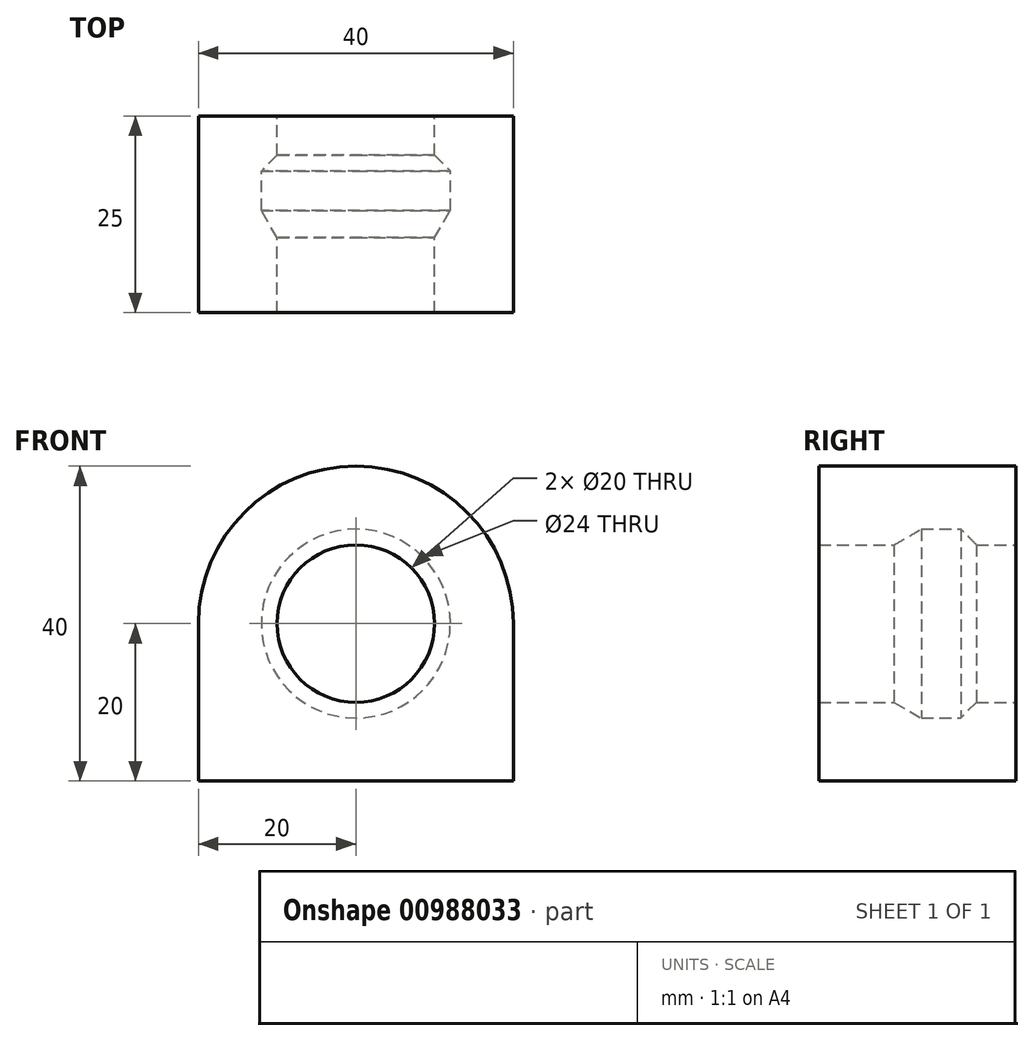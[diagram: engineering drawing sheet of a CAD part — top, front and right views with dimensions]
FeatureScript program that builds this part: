
annotation { "Feature Type Name" : "Feature", "Feature Type Description" : "" }
export const myFeature = defineFeature(function(context is Context, id is Id, definition is map)
    precondition{}
    {
        {
            assignVariable(context, id + "F0", {"name" : "length", "anyValue" : 25});
        }
        {
            var Q0;
            Q0=qCreatedBy(makeId("Front.planeOp"),FACE);
            var sketch = newSketch(context, id + "F1", { "sketchPlane" : qUnion([Q0])});
            skLineSegment(sketch, "E0.top", {"start": v(-20, -20) * mm, "end": v(20, -20) * mm});
            skLineSegment(sketch, "E0.left", {"start": v(-20, 0) * mm, "end": v(-20, -20) * mm});
            skLineSegment(sketch, "E0.right", {"start": v(20, 0) * mm, "end": v(20, -20) * mm});
            skPoint(sketch, "E0.middle", {"position": v(0, 0) * mm});
            skLineSegment(sketch, "E1", {"start": v(0, 0) * mm, "end": v(0, -20) * mm, "construction": true});
            skArc(sketch, "E2", {"start": v(-20, 0) * mm, "mid": v(0, 20) * mm, "end": v(20, 0) * mm});
            skSolve(sketch);
        }
        {
            var Q0;
            Q0=makeQuery(id+"F1.imprint","IMPRINT",FACE,{"disambiguationData":[TD([[makeQuery(id+"F1.imprint","IMPRINT",EDGE,{"derivedFrom":sQuery(id+"F1.wireOp",EDGE,"E0.top")}),1.0]])]});
            extrude(context, id + "F2", {"entities" : qUnion([Q0]), "endBound" : BoundingType.SYMMETRIC, "oppositeDirection" : true, "depth" : (getVariable(context, 'length')) * mm, "offsetDistance" : 25 * mm});
        }
        {
            var Q0;
            Q0=qCreatedBy(makeId("Right.planeOp"),FACE);
            var sketch = newSketch(context, id + "F3", { "sketchPlane" : qUnion([Q0])});
            skLineSegment(sketch, "E3", {"start": v(-67.48, 0) * mm, "end": v(42.56, 0) * mm});
            skSolve(sketch);
        }
        {
            var Q0;
            Q0=qCreatedBy(makeId("Right.planeOp"),FACE);
            var sketch = newSketch(context, id + "F4", { "sketchPlane" : qUnion([Q0])});
            skLineSegment(sketch, "E4", {"start": v(12.5, 10) * mm, "end": v(7.5, 10) * mm});
            skLineSegment(sketch, "E5", {"start": v(7.5, 10) * mm, "end": v(5.5, 12) * mm});
            skLineSegment(sketch, "E6", {"start": v(5.5, 12) * mm, "end": v(0.5, 12) * mm});
            skLineSegment(sketch, "E7", {"start": v(0.5, 12) * mm, "end": v(-2.96, 10) * mm});
            skLineSegment(sketch, "E8", {"start": v(-2.96, 10) * mm, "end": v(-12.5, 10) * mm});
            skLineSegment(sketch, "E9", {"start": v(12.5, 10) * mm, "end": v(12.5, 0) * mm});
            skLineSegment(sketch, "E10", {"start": v(12.5, 0) * mm, "end": v(-12.5, 0) * mm});
            skLineSegment(sketch, "E11", {"start": v(-12.5, 0) * mm, "end": v(-12.5, 10) * mm});
            skSolve(sketch);
        }
        {
            var Q0;
            Q0 = qSketchRegion(id + "F4", true);
            var Q1;
            Q1=sQuery(id+"F3.wireOp",EDGE,"E3");
            revolve(context, id + "F5", {"operationType" : NewBodyOperationType.REMOVE, "surfaceOperationType" : NewSurfaceOperationType.NEW, "entities" : qUnion([Q0]), "axis" : qUnion([Q1]), "revolveType" : RevolveType.FULL, "oppositeDirection" : true});
        }
    });
